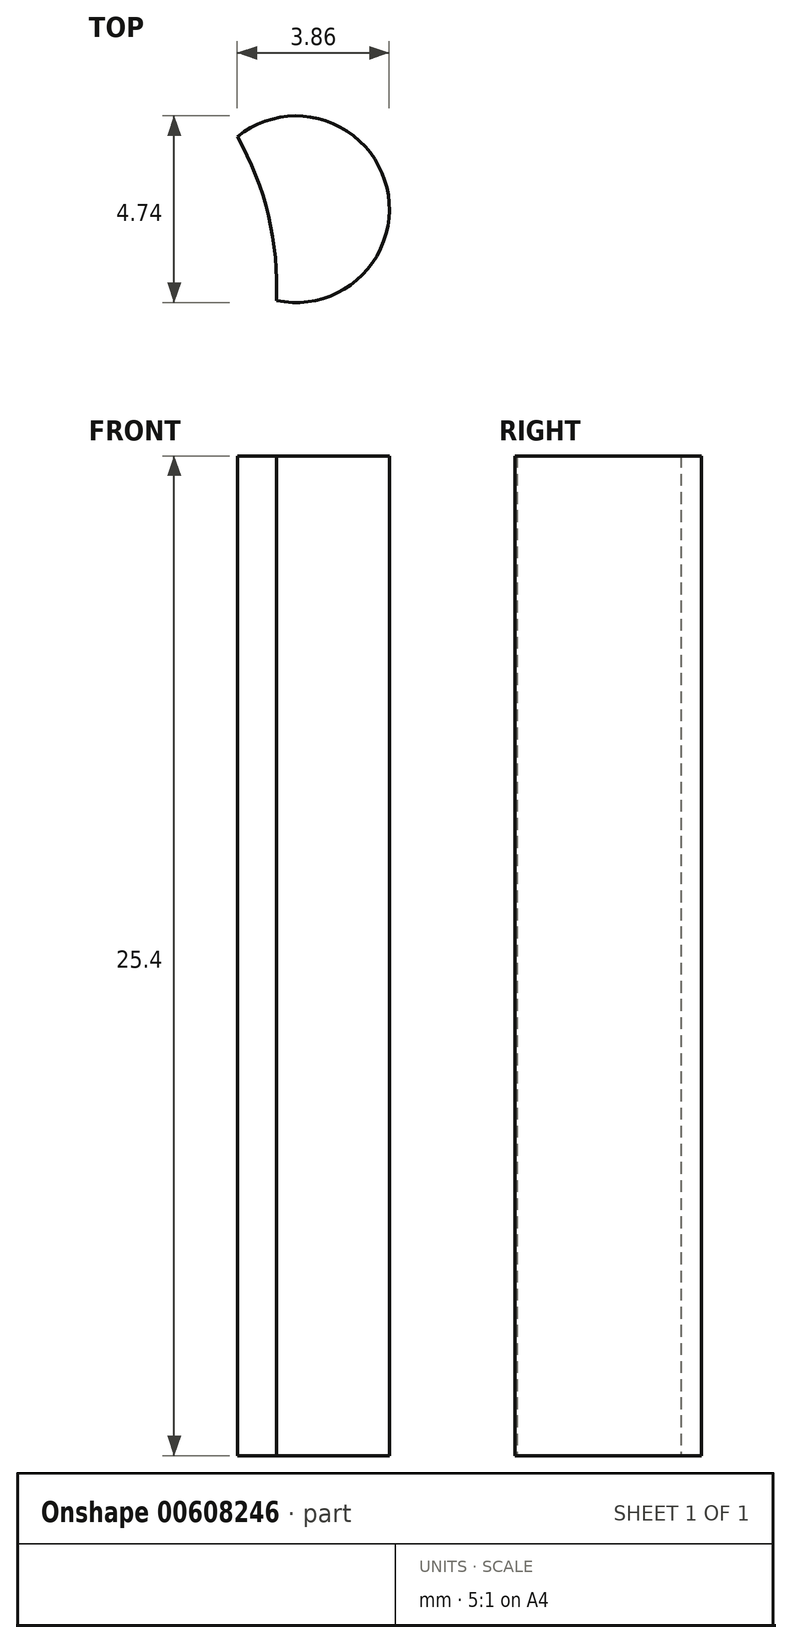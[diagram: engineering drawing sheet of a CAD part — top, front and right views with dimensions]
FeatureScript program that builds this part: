
annotation { "Feature Type Name" : "Feature", "Feature Type Description" : "" }
export const myFeature = defineFeature(function(context is Context, id is Id, definition is map)
    precondition{}
    {
        {
            var Q0;
            Q0=qCreatedBy(makeId("Top.planeOp"),FACE);
            var sketch = newSketch(context, id + "F0", { "sketchPlane" : qUnion([Q0])});
            skCircle(sketch, "E0", {"center": v(0, 0) * mm, "radius": 12.7 * mm, "construction": true});
            skCircle(sketch, "E1", {"center": v(0, 0) * mm, "radius": 9.53 * mm, "construction": true});
            skPoint(sketch, "E2.orphan", {"position": v(0, -17.99) * mm});
            skLineSegment(sketch, "E3", {"start": v(0, 43.77) * mm, "end": v(0, -22.8) * mm, "construction": true});
            skPoint(sketch, "E4.orphan", {"position": v(23.88, 0) * mm});
            skArc(sketch, "E5", {"start": v(9.52, 0.07) * mm, "mid": v(12.33, 2.94) * mm, "end": v(8.53, 4.23) * mm});
            skArc(sketch, "E6", {"start": v(9.52, 0.07) * mm, "mid": v(9.32, 2.22) * mm, "end": v(8.53, 4.23) * mm});
            skSolve(sketch);
        }
        {
            var Q0;
            Q0=makeQuery(id+"F0.imprint","IMPRINT",FACE,{"disambiguationData":[TD([[makeQuery(id+"F0.imprint","IMPRINT",EDGE,{"derivedFrom":sQuery(id+"F0.wireOp",EDGE,"E5")}),1.0]])]});
            var Q1;
            Q1=sQuery(id+"F0.wireOp",EDGE,"E6");
            extrude(context, id + "F1", {"entities" : qUnion([Q0]), "surfaceEntities" : qUnion([Q1]), "depth" : 25.4 * mm, "offsetDistance" : 25.4 * mm});
        }
    });
